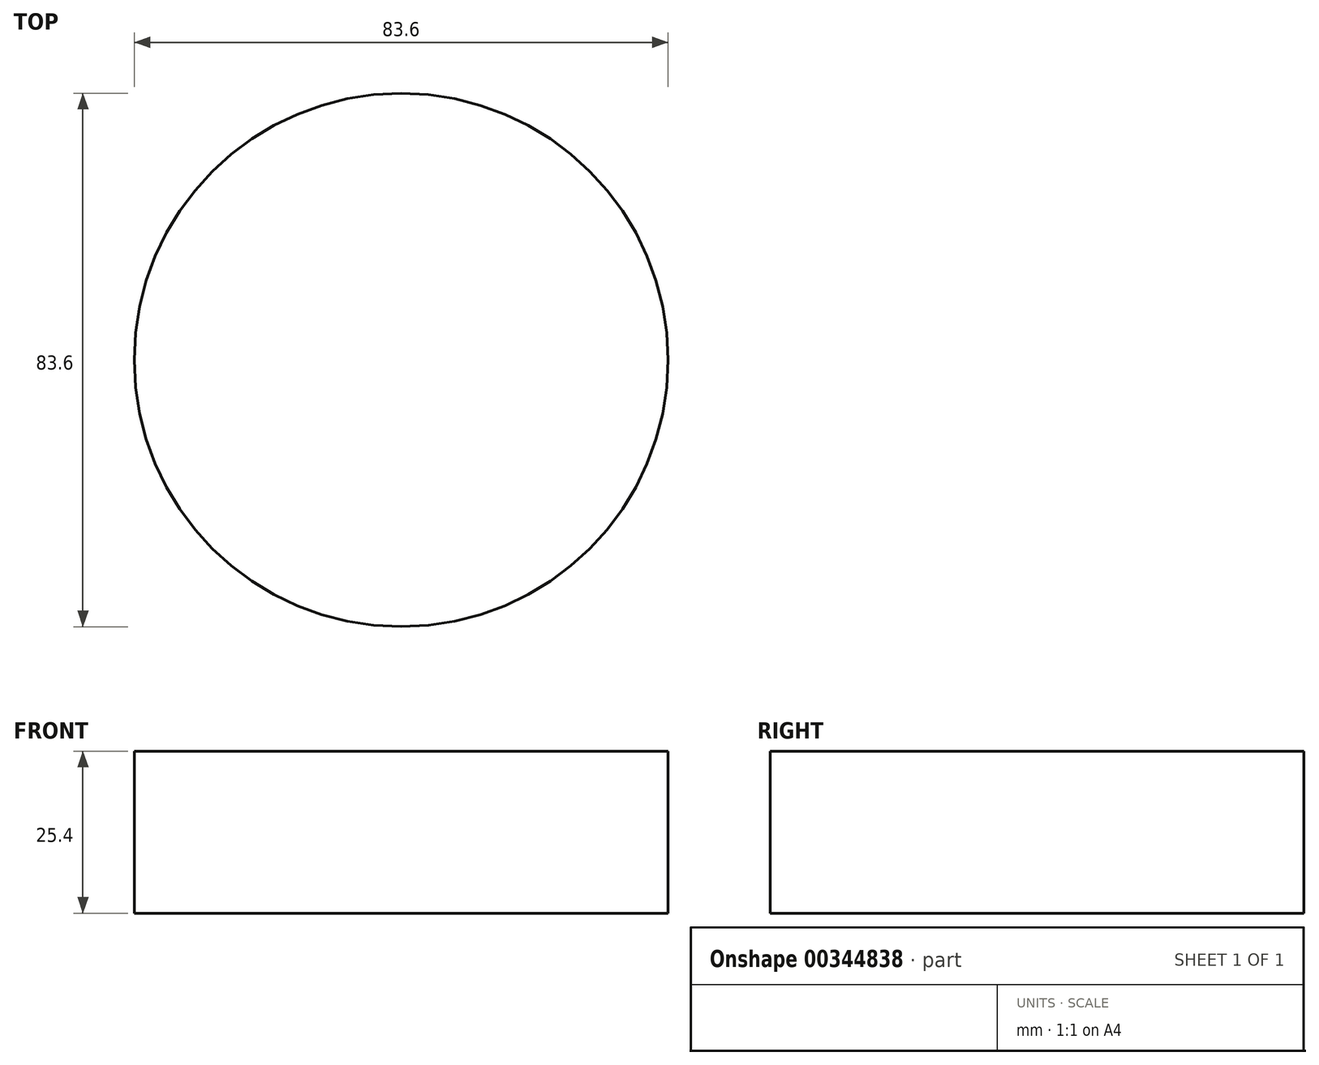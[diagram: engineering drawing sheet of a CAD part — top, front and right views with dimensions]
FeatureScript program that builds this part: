
annotation { "Feature Type Name" : "Feature", "Feature Type Description" : "" }
export const myFeature = defineFeature(function(context is Context, id is Id, definition is map)
    precondition{}
    {
        {
            var Q0;
            Q0=qCreatedBy(makeId("Top.planeOp"),FACE);
            var sketch = newSketch(context, id + "F0", { "sketchPlane" : qUnion([Q0])});
            skCircle(sketch, "E0", {"center": v(0, 0) * mm, "radius": 41.8 * mm});
            skSolve(sketch);
        }
        {
            var Q0;
            Q0 = qSketchRegion(id + "F0", true);
            extrude(context, id + "F1", {"entities" : qUnion([Q0]), "depth" : 25.4 * mm});
        }
    });
